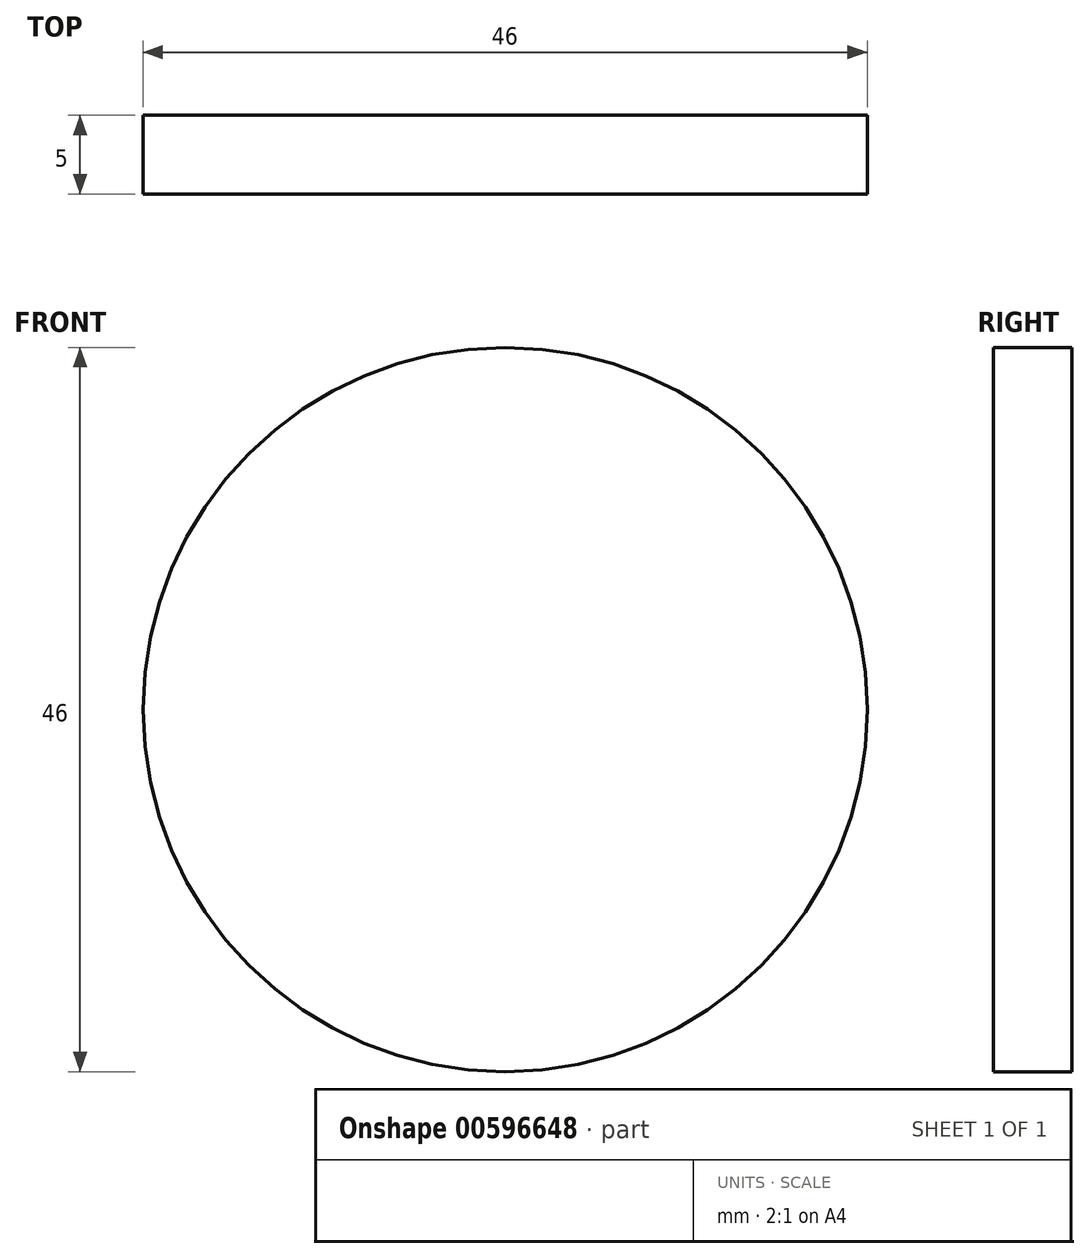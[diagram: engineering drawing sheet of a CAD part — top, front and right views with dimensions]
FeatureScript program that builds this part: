
annotation { "Feature Type Name" : "Feature", "Feature Type Description" : "" }
export const myFeature = defineFeature(function(context is Context, id is Id, definition is map)
    precondition{}
    {
        {
            var Q0;
            Q0=qCreatedBy(makeId("Front.planeOp"),FACE);
            var sketch = newSketch(context, id + "F0", { "sketchPlane" : qUnion([Q0])});
            skCircle(sketch, "E0", {"center": v(0, 0) * mm, "radius": 23 * mm});
            skSolve(sketch);
        }
        {
            var Q0;
            Q0=makeQuery(id+"F0.imprint","IMPRINT",FACE,{"disambiguationData":[TD([[makeQuery(id+"F0.imprint","IMPRINT",EDGE,{"derivedFrom":sQuery(id+"F0.wireOp",EDGE,"E0")}),1.0]])]});
            extrude(context, id + "F1", {"entities" : qUnion([Q0]), "depth" : 5 * mm, "offsetDistance" : 25 * mm});
        }
    });
